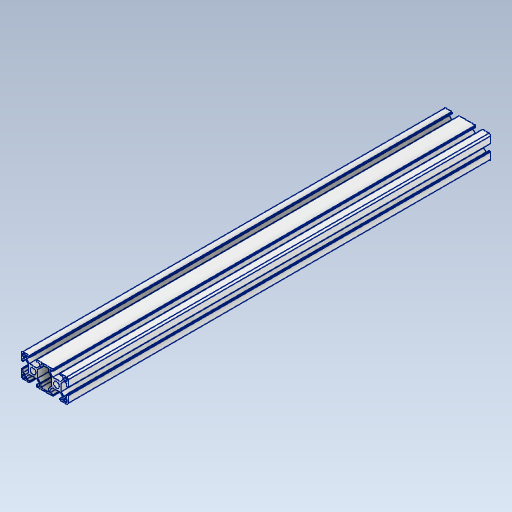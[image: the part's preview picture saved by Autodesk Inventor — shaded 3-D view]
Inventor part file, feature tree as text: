
AUTODESK INVENTOR PART (.ipt)
format: ipt  version: 2020.2 (Build 242310000, 310)  size: 296,960 bytes
history: native  units: mm
features: extrude x1, sketch x1
ambient origin geometry x8: Origin, YZ Plane, XZ Plane, XY Plane, X Axis, Y Axis, Z Axis, Center Point
bodies: Solid1 (feature_tree)
feature tree (2):
  extrude  "Extrusion1"  [1 undecoded]
  sketch  "Sketch1"  dims[d0=540.0mm d1=0.0mm]
note: 1 required parameter value undecoded (feature->parameter linkage not recoverable at this tier; creation-order binding heuristic only, values carry confidence <= 0.55)
